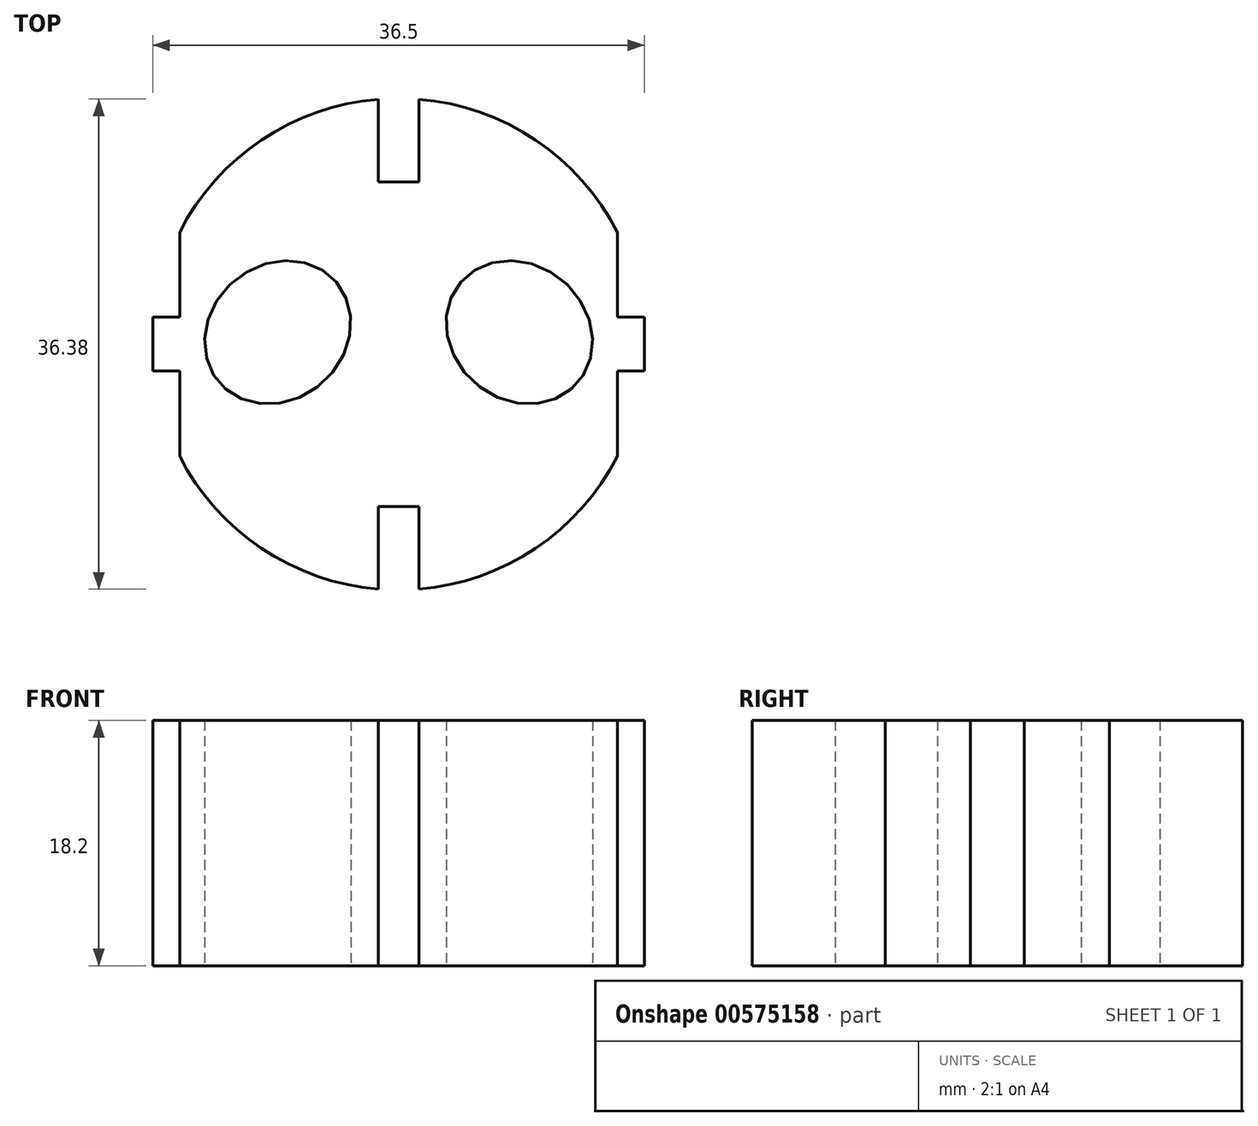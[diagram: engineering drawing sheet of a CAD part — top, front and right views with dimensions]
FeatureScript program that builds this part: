
annotation { "Feature Type Name" : "Feature", "Feature Type Description" : "" }
export const myFeature = defineFeature(function(context is Context, id is Id, definition is map)
    precondition{}
    {
        {
            var Q0;
            Q0=qCreatedBy(makeId("Top.planeOp"),FACE);
            var sketch = newSketch(context, id + "F0", { "sketchPlane" : qUnion([Q0])});
            skArc(sketch, "E0", {"start": v(16.25, 8.3) * mm, "mid": v(10.16, 15.16) * mm, "end": v(1.5, 18.19) * mm});
            skCircle(sketch, "E1", {"center": v(0, 0) * mm, "radius": 16.25 * mm, "construction": true});
            skLineSegment(sketch, "E2", {"start": v(0, 20.44) * mm, "end": v(0, -20.48) * mm, "construction": true});
            skLineSegment(sketch, "E3", {"start": v(-16.25, 8.3) * mm, "end": v(-16.25, 2) * mm});
            skLineSegment(sketch, "E4.MirrorCS", {"start": v(16.25, 8.3) * mm, "end": v(16.25, 2) * mm});
            skPoint(sketch, "E5.orphan", {"position": v(-16.25, 25.95) * mm});
            skPoint(sketch, "E6.orphan", {"position": v(16.25, 25.95) * mm});
            skPoint(sketch, "E7.orphan", {"position": v(16.25, -32.27) * mm});
            skPoint(sketch, "E8.orphan", {"position": v(-16.25, -32.27) * mm});
            skArc(sketch, "E9.trimOffspring", {"start": v(-16.25, -8.3) * mm, "mid": v(-10.16, -15.16) * mm, "end": v(-1.5, -18.19) * mm});
            skLineSegment(sketch, "E10", {"start": v(-25.91, 0) * mm, "end": v(23.22, 0) * mm, "construction": true});
            skPoint(sketch, "E10.startSnap0", {"position": v(-16.25, 0) * mm});
            skLineSegment(sketch, "E11", {"start": v(-16.25, 0) * mm, "end": v(-18.25, 0) * mm});
            skLineSegment(sketch, "E12", {"start": v(-18.25, 0) * mm, "end": v(-18.25, -2) * mm});
            skLineSegment(sketch, "E13", {"start": v(-18.25, -2) * mm, "end": v(-16.25, -2) * mm});
            skLineSegment(sketch, "E14.MirrorCS", {"start": v(-18.25, 0) * mm, "end": v(-18.25, 2) * mm});
            skLineSegment(sketch, "E15.MirrorCS", {"start": v(-18.25, 2) * mm, "end": v(-16.25, 2) * mm});
            skLineSegment(sketch, "E16.MirrorCS", {"start": v(18.25, -2) * mm, "end": v(16.25, -2) * mm});
            skLineSegment(sketch, "E17.MirrorCS", {"start": v(18.25, 0) * mm, "end": v(18.25, -2) * mm});
            skLineSegment(sketch, "E18.MirrorCS", {"start": v(18.25, 2) * mm, "end": v(16.25, 2) * mm});
            skLineSegment(sketch, "E19.MirrorCS", {"start": v(18.25, 0) * mm, "end": v(18.25, 2) * mm});
            skLineSegment(sketch, "E20", {"start": v(0, 18.25) * mm, "end": v(0, 12.05) * mm});
            skLineSegment(sketch, "E21", {"start": v(0, 12.05) * mm, "end": v(-1.5, 12.05) * mm});
            skLineSegment(sketch, "E22", {"start": v(-1.5, 12.05) * mm, "end": v(-1.5, 18.19) * mm});
            skLineSegment(sketch, "E23.MirrorCS", {"start": v(0, 12.05) * mm, "end": v(1.5, 12.05) * mm});
            skLineSegment(sketch, "E24.MirrorCS", {"start": v(1.5, 12.05) * mm, "end": v(1.5, 18.19) * mm});
            skLineSegment(sketch, "E25.MirrorCS", {"start": v(0, -12.05) * mm, "end": v(-1.5, -12.05) * mm});
            skLineSegment(sketch, "E26.MirrorCS", {"start": v(0, -12.05) * mm, "end": v(1.5, -12.05) * mm});
            skLineSegment(sketch, "E27.MirrorCS", {"start": v(-1.5, -12.05) * mm, "end": v(-1.5, -18.19) * mm});
            skLineSegment(sketch, "E28.MirrorCS", {"start": v(1.5, -12.05) * mm, "end": v(1.5, -18.19) * mm});
            skArc(sketch, "E29.trimOffspring", {"start": v(-1.5, 18.19) * mm, "mid": v(-10.16, 15.16) * mm, "end": v(-16.25, 8.3) * mm});
            skArc(sketch, "E30.trimOffspring", {"start": v(1.5, -18.19) * mm, "mid": v(10.16, -15.16) * mm, "end": v(16.25, -8.3) * mm});
            skLineSegment(sketch, "E31.trimOffspring", {"start": v(-16.25, -2) * mm, "end": v(-16.25, -8.3) * mm});
            skLineSegment(sketch, "E32.trimOffspring", {"start": v(16.25, -2) * mm, "end": v(16.25, -8.3) * mm});
            skEllipse(sketch, "E33", {"center": v(-8.97, 0.88) * mm, "majorRadius": 5.73 * mm, "minorRadius": 5 * mm, "majorAxis": v(0.76, 0.65)});
            skEllipse(sketch, "E34.MirrorC", {"center": v(8.97, 0.88) * mm, "majorRadius": 5.73 * mm, "minorRadius": 5 * mm, "majorAxis": v(-0.76, 0.65)});
            skSolve(sketch);
        }
        {
            var Q0;
            Q0=makeQuery(id+"F0.imprint","IMPRINT",FACE,{"disambiguationData":[TD([[makeQuery(id+"F0.imprint","IMPRINT",EDGE,{"derivedFrom":sQuery(id+"F0.wireOp",EDGE,"E0")}),1.0]])]});
            extrude(context, id + "F1", {"entities" : qUnion([Q0]), "depth" : 18.2 * mm, "offsetDistance" : 25 * mm});
        }
    });
